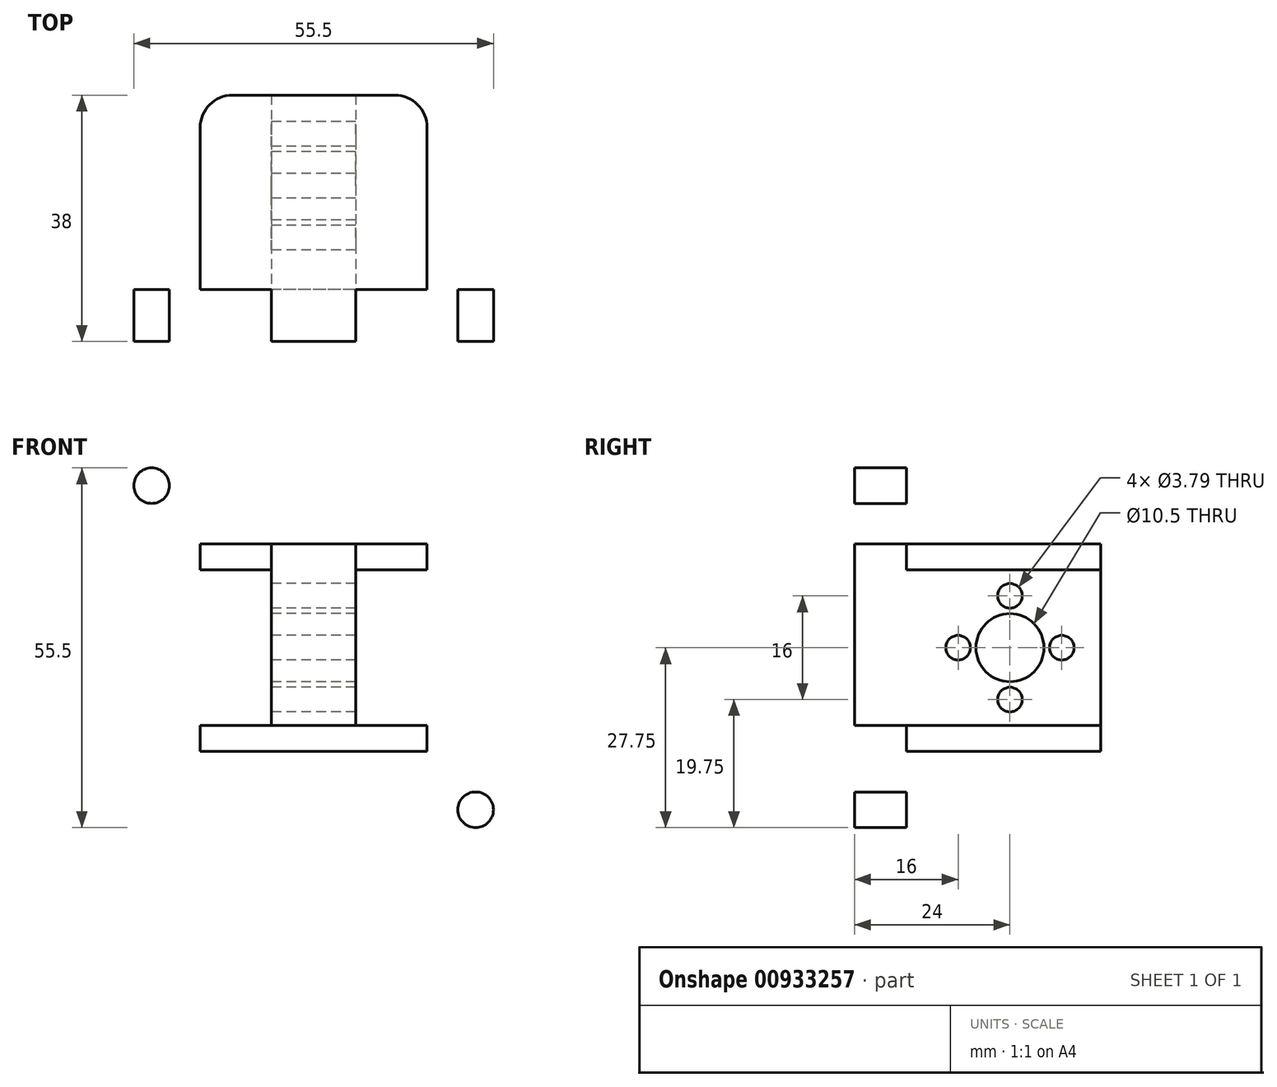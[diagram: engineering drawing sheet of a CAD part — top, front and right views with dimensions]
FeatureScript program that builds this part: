
annotation { "Feature Type Name" : "Feature", "Feature Type Description" : "" }
export const myFeature = defineFeature(function(context is Context, id is Id, definition is map)
    precondition{}
    {
        {
            var Q0;
            Q0=qCreatedBy(makeId("Front.planeOp"),FACE);
            var sketch = newSketch(context, id + "F0", { "sketchPlane" : qUnion([Q0])});
            skLineSegment(sketch, "E0.bottom", {"start": v(0, 0) * mm, "end": v(70, 0) * mm});
            skLineSegment(sketch, "E0.top", {"start": v(0, 130) * mm, "end": v(70, 130) * mm});
            skLineSegment(sketch, "E0.left", {"start": v(0, 0) * mm, "end": v(0, 130) * mm});
            skLineSegment(sketch, "E0.right", {"start": v(70, 0) * mm, "end": v(70, 130) * mm});
            skLineSegment(sketch, "E1", {"start": v(0, 125.15) * mm, "end": v(70, 125.15) * mm, "construction": true});
            skLineSegment(sketch, "E2", {"start": v(0, 101.15) * mm, "end": v(70, 101.15) * mm, "construction": true});
            skLineSegment(sketch, "E3", {"start": v(24, 130) * mm, "end": v(24, 78.99) * mm, "construction": true});
            skLineSegment(sketch, "E4", {"start": v(6, 130) * mm, "end": v(6, 79.2) * mm, "construction": true});
            skLineSegment(sketch, "E5", {"start": v(35, 130) * mm, "end": v(35, 0) * mm, "construction": true});
            skCircle(sketch, "E6", {"center": v(6, 125.15) * mm, "radius": 2.25 * mm});
            skCircle(sketch, "E7", {"center": v(24, 125.15) * mm, "radius": 2.25 * mm});
            skCircle(sketch, "E8", {"center": v(24, 101.15) * mm, "radius": 2.25 * mm});
            skCircle(sketch, "E9", {"center": v(6, 101.15) * mm, "radius": 2.25 * mm});
            skCircle(sketch, "E10.MirrorC", {"center": v(46, 101.15) * mm, "radius": 2.25 * mm});
            skCircle(sketch, "E11.MirrorC", {"center": v(64, 101.15) * mm, "radius": 2.25 * mm});
            skCircle(sketch, "E12.MirrorC", {"center": v(64, 125.15) * mm, "radius": 2.25 * mm});
            skCircle(sketch, "E13.MirrorC", {"center": v(46, 125.15) * mm, "radius": 2.25 * mm});
            skLineSegment(sketch, "E14", {"start": v(0, 65) * mm, "end": v(70, 65) * mm, "construction": true});
            skCircle(sketch, "E15.MirrorC", {"center": v(6, 28.85) * mm, "radius": 2.25 * mm});
            skCircle(sketch, "E16.MirrorC", {"center": v(24, 28.85) * mm, "radius": 2.25 * mm});
            skCircle(sketch, "E17.MirrorC", {"center": v(64, 28.85) * mm, "radius": 2.25 * mm});
            skCircle(sketch, "E18.MirrorC", {"center": v(46, 28.85) * mm, "radius": 2.25 * mm});
            skCircle(sketch, "E19.MirrorC", {"center": v(46, 4.85) * mm, "radius": 2.25 * mm});
            skCircle(sketch, "E20.MirrorC", {"center": v(64, 4.85) * mm, "radius": 2.25 * mm});
            skCircle(sketch, "E21.MirrorC", {"center": v(24, 4.85) * mm, "radius": 2.25 * mm});
            skCircle(sketch, "E22.MirrorC", {"center": v(6, 4.85) * mm, "radius": 2.25 * mm});
            skSolve(sketch);
        }
        {
            var Q0;
            Q0=makeQuery(id+"F0.imprint","IMPRINT",FACE,{"disambiguationData":[TD([[makeQuery(id+"F0.imprint","IMPRINT",EDGE,{"derivedFrom":sQuery(id+"F0.wireOp",EDGE,"E0.bottom")}),1.0]])]});
            extrude(context, id + "F1", {"entities" : qUnion([Q0]), "oppositeDirection" : true, "depth" : 8 * mm, "offsetDistance" : 25 * mm});
        }
        {
            var Q0;
            Q0=makeQuery(id+"F1.opExtrude","CAP_FACE",FACE,{"disambiguationData":[OSD([sQuery(id+"F0.wireOp",EDGE,"E0.bottom"),sQuery(id+"F0.wireOp",EDGE,"E0.top"),sQuery(id+"F0.wireOp",EDGE,"E0.left"),sQuery(id+"F0.wireOp",EDGE,"E0.right"),sQuery(id+"F0.wireOp",EDGE,"E6"),sQuery(id+"F0.wireOp",EDGE,"E7"),sQuery(id+"F0.wireOp",EDGE,"E8"),sQuery(id+"F0.wireOp",EDGE,"E9"),sQuery(id+"F0.wireOp",EDGE,"E10.MirrorC"),sQuery(id+"F0.wireOp",EDGE,"E11.MirrorC"),sQuery(id+"F0.wireOp",EDGE,"E12.MirrorC"),sQuery(id+"F0.wireOp",EDGE,"E13.MirrorC"),sQuery(id+"F0.wireOp",EDGE,"E15.MirrorC"),sQuery(id+"F0.wireOp",EDGE,"E16.MirrorC"),sQuery(id+"F0.wireOp",EDGE,"E17.MirrorC"),sQuery(id+"F0.wireOp",EDGE,"E18.MirrorC"),sQuery(id+"F0.wireOp",EDGE,"E19.MirrorC"),sQuery(id+"F0.wireOp",EDGE,"E20.MirrorC"),sQuery(id+"F0.wireOp",EDGE,"E21.MirrorC"),sQuery(id+"F0.wireOp",EDGE,"E22.MirrorC")])],"isStart":true});
            var sketch = newSketch(context, id + "F2", { "sketchPlane" : qUnion([Q0])});
            skCircle(sketch, "E23", {"center": v(6, 125.15) * mm, "radius": 3.75 * mm});
            skCircle(sketch, "E24", {"center": v(24, 125.15) * mm, "radius": 3.75 * mm});
            skCircle(sketch, "E25", {"center": v(6, 101.15) * mm, "radius": 3.75 * mm});
            skCircle(sketch, "E26", {"center": v(24, 101.15) * mm, "radius": 3.75 * mm});
            skLineSegment(sketch, "E27", {"start": v(35, 130) * mm, "end": v(35, 0) * mm});
            skLineSegment(sketch, "E28", {"start": v(0, 65) * mm, "end": v(70, 65) * mm});
            skCircle(sketch, "E29.MirrorC", {"center": v(46, 101.15) * mm, "radius": 3.75 * mm});
            skCircle(sketch, "E30.MirrorC", {"center": v(64, 101.15) * mm, "radius": 3.75 * mm});
            skCircle(sketch, "E31.MirrorC", {"center": v(46, 125.15) * mm, "radius": 3.75 * mm});
            skCircle(sketch, "E32.MirrorC", {"center": v(64, 125.15) * mm, "radius": 3.75 * mm});
            skCircle(sketch, "E33.MirrorC", {"center": v(6, 28.85) * mm, "radius": 3.75 * mm});
            skCircle(sketch, "E34.MirrorC", {"center": v(24, 28.85) * mm, "radius": 3.75 * mm});
            skCircle(sketch, "E35.MirrorC", {"center": v(46, 28.85) * mm, "radius": 3.75 * mm});
            skCircle(sketch, "E36.MirrorC", {"center": v(64, 28.85) * mm, "radius": 3.75 * mm});
            skCircle(sketch, "E37.MirrorC", {"center": v(64, 4.85) * mm, "radius": 3.75 * mm});
            skCircle(sketch, "E38.MirrorC", {"center": v(46, 4.85) * mm, "radius": 3.75 * mm});
            skCircle(sketch, "E39.MirrorC", {"center": v(24, 4.85) * mm, "radius": 3.75 * mm});
            skCircle(sketch, "E40.MirrorC", {"center": v(6, 4.85) * mm, "radius": 3.75 * mm});
            skSolve(sketch);
        }
        {
            var Q0;
            Q0=makeQuery(id+"F1.opExtrude","CAP_FACE",FACE,{"disambiguationData":[OSD([sQuery(id+"F0.wireOp",EDGE,"E0.bottom"),sQuery(id+"F0.wireOp",EDGE,"E0.top"),sQuery(id+"F0.wireOp",EDGE,"E0.left"),sQuery(id+"F0.wireOp",EDGE,"E0.right"),sQuery(id+"F0.wireOp",EDGE,"E6"),sQuery(id+"F0.wireOp",EDGE,"E7"),sQuery(id+"F0.wireOp",EDGE,"E8"),sQuery(id+"F0.wireOp",EDGE,"E9"),sQuery(id+"F0.wireOp",EDGE,"E10.MirrorC"),sQuery(id+"F0.wireOp",EDGE,"E11.MirrorC"),sQuery(id+"F0.wireOp",EDGE,"E12.MirrorC"),sQuery(id+"F0.wireOp",EDGE,"E13.MirrorC"),sQuery(id+"F0.wireOp",EDGE,"E15.MirrorC"),sQuery(id+"F0.wireOp",EDGE,"E16.MirrorC"),sQuery(id+"F0.wireOp",EDGE,"E17.MirrorC"),sQuery(id+"F0.wireOp",EDGE,"E18.MirrorC"),sQuery(id+"F0.wireOp",EDGE,"E19.MirrorC"),sQuery(id+"F0.wireOp",EDGE,"E20.MirrorC"),sQuery(id+"F0.wireOp",EDGE,"E21.MirrorC"),sQuery(id+"F0.wireOp",EDGE,"E22.MirrorC")])],"isStart":false});
            var sketch = newSketch(context, id + "F3", { "sketchPlane" : qUnion([Q0])});
            skLineSegment(sketch, "E41.bottom", {"start": v(-28.5, 53) * mm, "end": v(-41.5, 53) * mm});
            skLineSegment(sketch, "E41.top", {"start": v(-28.5, 77) * mm, "end": v(-41.5, 77) * mm});
            skLineSegment(sketch, "E41.left", {"start": v(-28.5, 53) * mm, "end": v(-28.5, 77) * mm});
            skLineSegment(sketch, "E41.right", {"start": v(-41.5, 53) * mm, "end": v(-41.5, 77) * mm});
            skPoint(sketch, "E41.middle", {"position": v(-35, 65) * mm});
            skSolve(sketch);
        }
        {
            var Q0;
            Q0=makeQuery(id+"F3.imprint","IMPRINT",FACE,{"disambiguationData":[TD([[makeQuery(id+"F3.imprint","IMPRINT",EDGE,{"derivedFrom":sQuery(id+"F3.wireOp",EDGE,"E41.bottom")}),-1.0]])]});
            extrude(context, id + "F4", {"entities" : qUnion([Q0]), "operationType" : NewBodyOperationType.ADD, "depth" : 30 * mm, "offsetDistance" : 25 * mm});
        }
        {
            var Q0;
            Q0=makeQuery(id+"F4.opExtrude","SWEPT_FACE",FACE,{"disambiguationData":[OSD([sQuery(id+"F3.wireOp",EDGE,"E41.left")])]});
            var sketch = newSketch(context, id + "F5", { "sketchPlane" : qUnion([Q0])});
            skLineSegment(sketch, "E42", {"start": v(-24, 81.62) * mm, "end": v(-24, 48.38) * mm, "construction": true});
            skLineSegment(sketch, "E43", {"start": v(-38, 65) * mm, "end": v(-8, 65) * mm, "construction": true});
            skCircle(sketch, "E44", {"center": v(-24, 65) * mm, "radius": 5.25 * mm});
            skPoint(sketch, "E44.centerSnap0", {"position": v(-24, 65) * mm});
            skCircle(sketch, "E45", {"center": v(-24, 65) * mm, "radius": 11.1 * mm, "construction": true});
            skCircle(sketch, "E46", {"center": v(-24, 65) * mm, "radius": 8 * mm, "construction": true});
            skCircle(sketch, "E47", {"center": v(-24, 73) * mm, "radius": 1.9 * mm});
            skCircle(sketch, "E48.1.0", {"center": v(-32, 65) * mm, "radius": 1.9 * mm});
            skCircle(sketch, "E48.2.0", {"center": v(-24, 57) * mm, "radius": 1.9 * mm});
            skCircle(sketch, "E48.3.0", {"center": v(-16, 65) * mm, "radius": 1.9 * mm});
            skSolve(sketch);
        }
        {
            var Q0;
            Q0=makeQuery(id+"F5.imprint","IMPRINT",FACE,{"disambiguationData":[TD([[makeQuery(id+"F5.imprint","IMPRINT",EDGE,{"derivedFrom":sQuery(id+"F5.wireOp",EDGE,"E48.1.0")}),1.0]])]});
            var Q1;
            Q1=makeQuery(id+"F5.imprint","IMPRINT",FACE,{"disambiguationData":[TD([[makeQuery(id+"F5.imprint","IMPRINT",EDGE,{"derivedFrom":sQuery(id+"F5.wireOp",EDGE,"E47")}),1.0]])]});
            var Q2;
            Q2=makeQuery(id+"F5.imprint","IMPRINT",FACE,{"disambiguationData":[TD([[makeQuery(id+"F5.imprint","IMPRINT",EDGE,{"derivedFrom":sQuery(id+"F5.wireOp",EDGE,"E48.3.0")}),1.0]])]});
            var Q3;
            Q3=makeQuery(id+"F5.imprint","IMPRINT",FACE,{"disambiguationData":[TD([[makeQuery(id+"F5.imprint","IMPRINT",EDGE,{"derivedFrom":sQuery(id+"F5.wireOp",EDGE,"E48.2.0")}),1.0]])]});
            var Q4;
            Q4=makeQuery(id+"F5.imprint","IMPRINT",FACE,{"disambiguationData":[TD([[makeQuery(id+"F5.imprint","IMPRINT",EDGE,{"derivedFrom":sQuery(id+"F5.wireOp",EDGE,"E44")}),1.0]])]});
            extrude(context, id + "F6", {"entities" : qUnion([Q0, Q1, Q2, Q3, Q4]), "operationType" : NewBodyOperationType.REMOVE, "endBound" : BoundingType.THROUGH_ALL, "oppositeDirection" : true, "depth" : 25 * mm, "offsetDistance" : 25 * mm});
        }
        {
            var Q0;
            Q0=makeQuery(id+"F1.opExtrude","CAP_FACE",FACE,{"disambiguationData":[OSD([sQuery(id+"F0.wireOp",EDGE,"E0.bottom"),sQuery(id+"F0.wireOp",EDGE,"E0.top"),sQuery(id+"F0.wireOp",EDGE,"E0.left"),sQuery(id+"F0.wireOp",EDGE,"E0.right"),sQuery(id+"F0.wireOp",EDGE,"E6"),sQuery(id+"F0.wireOp",EDGE,"E7"),sQuery(id+"F0.wireOp",EDGE,"E8"),sQuery(id+"F0.wireOp",EDGE,"E9"),sQuery(id+"F0.wireOp",EDGE,"E10.MirrorC"),sQuery(id+"F0.wireOp",EDGE,"E11.MirrorC"),sQuery(id+"F0.wireOp",EDGE,"E12.MirrorC"),sQuery(id+"F0.wireOp",EDGE,"E13.MirrorC"),sQuery(id+"F0.wireOp",EDGE,"E15.MirrorC"),sQuery(id+"F0.wireOp",EDGE,"E16.MirrorC"),sQuery(id+"F0.wireOp",EDGE,"E17.MirrorC"),sQuery(id+"F0.wireOp",EDGE,"E18.MirrorC"),sQuery(id+"F0.wireOp",EDGE,"E19.MirrorC"),sQuery(id+"F0.wireOp",EDGE,"E20.MirrorC"),sQuery(id+"F0.wireOp",EDGE,"E21.MirrorC"),sQuery(id+"F0.wireOp",EDGE,"E22.MirrorC")])],"isStart":false});
            var sketch = newSketch(context, id + "F7", { "sketchPlane" : qUnion([Q0])});
            skLineSegment(sketch, "E49", {"start": v(-60, 130) * mm, "end": v(-60, 0) * mm, "construction": true});
            skLineSegment(sketch, "E50", {"start": v(-70, 90) * mm, "end": v(0, 90) * mm, "construction": true});
            skCircle(sketch, "E51", {"center": v(-60, 90) * mm, "radius": 2.75 * mm});
            skCircle(sketch, "E52.MirrorC", {"center": v(-10, 90) * mm, "radius": 2.75 * mm});
            skCircle(sketch, "E53.MirrorC", {"center": v(-10, 40) * mm, "radius": 2.75 * mm});
            skCircle(sketch, "E54.MirrorC", {"center": v(-60, 40) * mm, "radius": 2.75 * mm});
            skSolve(sketch);
        }
        {
            var Q0;
            Q0=makeQuery(id+"F7.imprint","IMPRINT",FACE,{"disambiguationData":[TD([[makeQuery(id+"F7.imprint","IMPRINT",EDGE,{"derivedFrom":sQuery(id+"F7.wireOp",EDGE,"E51")}),1.0]])]});
            var Q1;
            Q1=makeQuery(id+"F7.imprint","IMPRINT",FACE,{"disambiguationData":[TD([[makeQuery(id+"F7.imprint","IMPRINT",EDGE,{"derivedFrom":sQuery(id+"F7.wireOp",EDGE,"E52.MirrorC")}),-1.0]])]});
            var Q2;
            Q2=makeQuery(id+"F7.imprint","IMPRINT",FACE,{"disambiguationData":[TD([[makeQuery(id+"F7.imprint","IMPRINT",EDGE,{"derivedFrom":sQuery(id+"F7.wireOp",EDGE,"E54.MirrorC")}),-1.0]])]});
            var Q3;
            Q3=makeQuery(id+"F7.imprint","IMPRINT",FACE,{"disambiguationData":[TD([[makeQuery(id+"F7.imprint","IMPRINT",EDGE,{"derivedFrom":sQuery(id+"F7.wireOp",EDGE,"E53.MirrorC")}),1.0]])]});
            extrude(context, id + "F8", {"entities" : qUnion([Q0, Q1, Q2, Q3]), "operationType" : NewBodyOperationType.REMOVE, "endBound" : BoundingType.THROUGH_ALL, "oppositeDirection" : true, "depth" : 25 * mm, "offsetDistance" : 25 * mm});
        }
        {
            var Q0;
            Q0=makeQuery(id+"F1.opExtrude","CAP_FACE",FACE,{"disambiguationData":[OSD([sQuery(id+"F0.wireOp",EDGE,"E0.bottom"),sQuery(id+"F0.wireOp",EDGE,"E0.top"),sQuery(id+"F0.wireOp",EDGE,"E0.left"),sQuery(id+"F0.wireOp",EDGE,"E0.right"),sQuery(id+"F0.wireOp",EDGE,"E6"),sQuery(id+"F0.wireOp",EDGE,"E7"),sQuery(id+"F0.wireOp",EDGE,"E8"),sQuery(id+"F0.wireOp",EDGE,"E9"),sQuery(id+"F0.wireOp",EDGE,"E10.MirrorC"),sQuery(id+"F0.wireOp",EDGE,"E11.MirrorC"),sQuery(id+"F0.wireOp",EDGE,"E12.MirrorC"),sQuery(id+"F0.wireOp",EDGE,"E13.MirrorC"),sQuery(id+"F0.wireOp",EDGE,"E15.MirrorC"),sQuery(id+"F0.wireOp",EDGE,"E16.MirrorC"),sQuery(id+"F0.wireOp",EDGE,"E17.MirrorC"),sQuery(id+"F0.wireOp",EDGE,"E18.MirrorC"),sQuery(id+"F0.wireOp",EDGE,"E19.MirrorC"),sQuery(id+"F0.wireOp",EDGE,"E20.MirrorC"),sQuery(id+"F0.wireOp",EDGE,"E21.MirrorC"),sQuery(id+"F0.wireOp",EDGE,"E22.MirrorC")])],"isStart":false});
            var sketch = newSketch(context, id + "F9", { "sketchPlane" : qUnion([Q0])});
            skCircle(sketch, "E55", {"center": v(-60, 90) * mm, "radius": 5 * mm});
            skCircle(sketch, "E56.MirrorC", {"center": v(-10, 90) * mm, "radius": 5 * mm});
            skCircle(sketch, "E57.MirrorC", {"center": v(-10, 40) * mm, "radius": 5 * mm});
            skCircle(sketch, "E58.MirrorC", {"center": v(-60, 40) * mm, "radius": 5 * mm});
            skSolve(sketch);
        }
        {
            var Q0;
            Q0=makeQuery(id+"F9.imprint","IMPRINT",FACE,{"disambiguationData":[TD([[makeQuery(id+"F9.imprint","IMPRINT",EDGE,{"derivedFrom":sQuery(id+"F9.wireOp",EDGE,"E55")}),1.0]])]});
            var Q1;
            Q1=makeQuery(id+"F9.imprint","IMPRINT",FACE,{"disambiguationData":[TD([[makeQuery(id+"F9.imprint","IMPRINT",EDGE,{"derivedFrom":sQuery(id+"F9.wireOp",EDGE,"E56.MirrorC")}),-1.0]])]});
            var Q2;
            Q2=makeQuery(id+"F9.imprint","IMPRINT",FACE,{"disambiguationData":[TD([[makeQuery(id+"F9.imprint","IMPRINT",EDGE,{"derivedFrom":sQuery(id+"F9.wireOp",EDGE,"E57.MirrorC")}),1.0]])]});
            var Q3;
            Q3=makeQuery(id+"F9.imprint","IMPRINT",FACE,{"disambiguationData":[TD([[makeQuery(id+"F9.imprint","IMPRINT",EDGE,{"derivedFrom":sQuery(id+"F9.wireOp",EDGE,"E58.MirrorC")}),-1.0]])]});
            extrude(context, id + "F10", {"entities" : qUnion([Q0, Q1, Q2, Q3]), "operationType" : NewBodyOperationType.REMOVE, "oppositeDirection" : true, "depth" : 5 * mm, "offsetDistance" : 25 * mm});
        }
        {
            var Q0;
            Q0=makeQuery(id+"F4.opExtrude","SWEPT_FACE",FACE,{"disambiguationData":[OSD([sQuery(id+"F3.wireOp",EDGE,"E41.top")])]});
            var sketch = newSketch(context, id + "F11", { "sketchPlane" : qUnion([Q0])});
            skLineSegment(sketch, "E59", {"start": v(41.5, 38) * mm, "end": v(28.5, 38) * mm});
            skLineSegment(sketch, "E60.bottom", {"start": v(28.5, 38) * mm, "end": v(22.5, 38) * mm});
            skLineSegment(sketch, "E60.top", {"start": v(28.5, 8) * mm, "end": v(17.5, 8) * mm});
            skLineSegment(sketch, "E60.left", {"start": v(28.5, 38) * mm, "end": v(28.5, 8) * mm});
            skLineSegment(sketch, "E60.right", {"start": v(17.5, 33) * mm, "end": v(17.5, 8) * mm});
            skPoint(sketch, "E61.visualSharp", {"position": v(17.5, 38) * mm});
            skArc(sketch, "E61.filletArc", {"start": v(22.5, 38) * mm, "mid": v(18.96, 36.54) * mm, "end": v(17.5, 33) * mm});
            skLineSegment(sketch, "E62", {"start": v(35, 38) * mm, "end": v(35, 8) * mm, "construction": true});
            skLineSegment(sketch, "E63.MirrorCS", {"start": v(41.5, 38) * mm, "end": v(41.5, 8) * mm});
            skLineSegment(sketch, "E64.MirrorCS", {"start": v(41.5, 8) * mm, "end": v(52.5, 8) * mm});
            skLineSegment(sketch, "E65.MirrorCS", {"start": v(41.5, 38) * mm, "end": v(47.5, 38) * mm});
            skLineSegment(sketch, "E66.MirrorCS", {"start": v(52.5, 33) * mm, "end": v(52.5, 8) * mm});
            skArc(sketch, "E67.MirrorCS", {"start": v(47.5, 38) * mm, "mid": v(51.04, 36.54) * mm, "end": v(52.5, 33) * mm});
            skSolve(sketch);
        }
        {
            var Q0;
            {var subQ0=sQuery(id+"F11.wireOp",EDGE,"xESoRonm-LhQB-Ssj1-jqFH-StdoRr2X7NTl");Q0=makeQuery(id+"F11.imprint","IMPRINT",FACE,{"disambiguationData":[TD([[makeQuery(id+"F11.imprint","IMPRINT",EDGE,{"derivedFrom":subQ0}),1.0]])]});}
            var Q1;
            {var subQ6=sQuery(id+"F11.wireOp",EDGE,"E59");Q1=makeQuery(id+"F11.imprint","IMPRINT",FACE,{"disambiguationData":[TD([[makeQuery(id+"F11.imprint","IMPRINT",EDGE,{"derivedFrom":subQ6}),-1.0]])]});}
            var Q2;
            {var subQ0=sQuery(id+"F11.wireOp",EDGE,"kL0RBXTn-8g1l-G1Ez-Omut-TmTzhNwdl61b");Q2=makeQuery(id+"F11.imprint","IMPRINT",FACE,{"disambiguationData":[TD([[makeQuery(id+"F11.imprint","IMPRINT",EDGE,{"derivedFrom":subQ0}),1.0]])]});}
            extrude(context, id + "F12", {"entities" : qUnion([Q0, Q1, Q2]), "operationType" : NewBodyOperationType.ADD, "depth" : 4 * mm, "offsetDistance" : 25 * mm});
        }
        {
            var Q0;
            Q0=makeQuery(id+"F4.opExtrude","SWEPT_FACE",FACE,{"disambiguationData":[OSD([sQuery(id+"F3.wireOp",EDGE,"E41.bottom")])]});
            var sketch = newSketch(context, id + "F13", { "sketchPlane" : qUnion([Q0])});
            skLineSegment(sketch, "E68", {"start": v(52.5, -8) * mm, "end": v(17.5, -8) * mm});
            skLineSegment(sketch, "E69", {"start": v(28.5, -38) * mm, "end": v(41.5, -38) * mm});
            skLineSegment(sketch, "E70", {"start": v(35, -38) * mm, "end": v(35, -8) * mm, "construction": true});
            skLineSegment(sketch, "E71.bottom", {"start": v(41.5, -38) * mm, "end": v(47.5, -38) * mm});
            skLineSegment(sketch, "E71.top", {"start": v(41.5, -8) * mm, "end": v(52.5, -8) * mm});
            skLineSegment(sketch, "E71.left", {"start": v(41.5, -38) * mm, "end": v(41.5, -8) * mm});
            skLineSegment(sketch, "E71.right", {"start": v(52.5, -33) * mm, "end": v(52.5, -8) * mm});
            skLineSegment(sketch, "E72.MirrorCS", {"start": v(28.5, -8) * mm, "end": v(17.5, -8) * mm});
            skLineSegment(sketch, "E73.MirrorCS", {"start": v(28.5, -38) * mm, "end": v(22.5, -38) * mm});
            skPoint(sketch, "E74.orphan", {"position": v(0, -8) * mm});
            skPoint(sketch, "E75.visualSharp", {"position": v(52.5, -38) * mm});
            skArc(sketch, "E75.filletArc", {"start": v(47.5, -38) * mm, "mid": v(51.04, -36.54) * mm, "end": v(52.5, -33) * mm});
            skPoint(sketch, "E76.visualSharp", {"position": v(17.5, -38) * mm});
            skLineSegment(sketch, "E77.MirrorCS", {"start": v(28.5, -38) * mm, "end": v(28.5, -8) * mm});
            skLineSegment(sketch, "E78.MirrorCS", {"start": v(17.5, -33) * mm, "end": v(17.5, -8) * mm});
            skArc(sketch, "E79.MirrorCS", {"start": v(22.5, -38) * mm, "mid": v(18.96, -36.54) * mm, "end": v(17.5, -33) * mm});
            skSolve(sketch);
        }
        {
            var Q0;
            {var subQ0=sQuery(id+"F13.wireOp",EDGE,"hdJWUI9M-KXb4-t5Z4-sRnf-rSk5xYNh7SRG");Q0=makeQuery(id+"F13.imprint","IMPRINT",FACE,{"disambiguationData":[TD([[makeQuery(id+"F13.imprint","IMPRINT",EDGE,{"derivedFrom":subQ0}),1.0]])]});}
            var Q1;
            {var subQ6=sQuery(id+"F13.wireOp",EDGE,"E69");Q1=makeQuery(id+"F13.imprint","IMPRINT",FACE,{"disambiguationData":[TD([[makeQuery(id+"F13.imprint","IMPRINT",EDGE,{"derivedFrom":subQ6}),1.0]])]});}
            var Q2;
            {var subQ0=sQuery(id+"F13.wireOp",EDGE,"G3PmWDNW-oeGG-h8XP-9mMC-rU47nYxFmo2q");Q2=makeQuery(id+"F13.imprint","IMPRINT",FACE,{"disambiguationData":[TD([[makeQuery(id+"F13.imprint","IMPRINT",EDGE,{"derivedFrom":subQ0}),1.0]])]});}
            extrude(context, id + "F14", {"entities" : qUnion([Q0, Q1, Q2]), "operationType" : NewBodyOperationType.ADD, "depth" : 4 * mm, "offsetDistance" : 25 * mm});
        }
        {
            var Q0;
            Q0=makeQuery(id+"F1.opExtrude","CAP_FACE",FACE,{"disambiguationData":[OSD([sQuery(id+"F0.wireOp",EDGE,"E0.bottom"),sQuery(id+"F0.wireOp",EDGE,"E0.top"),sQuery(id+"F0.wireOp",EDGE,"E0.left"),sQuery(id+"F0.wireOp",EDGE,"E0.right"),sQuery(id+"F0.wireOp",EDGE,"E6"),sQuery(id+"F0.wireOp",EDGE,"E7"),sQuery(id+"F0.wireOp",EDGE,"E8"),sQuery(id+"F0.wireOp",EDGE,"E9"),sQuery(id+"F0.wireOp",EDGE,"E10.MirrorC"),sQuery(id+"F0.wireOp",EDGE,"E11.MirrorC"),sQuery(id+"F0.wireOp",EDGE,"E12.MirrorC"),sQuery(id+"F0.wireOp",EDGE,"E13.MirrorC"),sQuery(id+"F0.wireOp",EDGE,"E15.MirrorC"),sQuery(id+"F0.wireOp",EDGE,"E16.MirrorC"),sQuery(id+"F0.wireOp",EDGE,"E17.MirrorC"),sQuery(id+"F0.wireOp",EDGE,"E18.MirrorC"),sQuery(id+"F0.wireOp",EDGE,"E19.MirrorC"),sQuery(id+"F0.wireOp",EDGE,"E20.MirrorC"),sQuery(id+"F0.wireOp",EDGE,"E21.MirrorC"),sQuery(id+"F0.wireOp",EDGE,"E22.MirrorC")])],"isStart":true});
            var sketch = newSketch(context, id + "F15", { "sketchPlane" : qUnion([Q0])});
            skCircle(sketch, "E80", {"center": v(6, 125.15) * mm, "radius": 3.75 * mm});
            skCircle(sketch, "E81", {"center": v(24, 125.15) * mm, "radius": 3.75 * mm});
            skCircle(sketch, "E82", {"center": v(6, 101.15) * mm, "radius": 3.75 * mm});
            skCircle(sketch, "E83", {"center": v(24, 101.15) * mm, "radius": 3.75 * mm});
            skLineSegment(sketch, "E84", {"start": v(35, 130) * mm, "end": v(35, 0) * mm, "construction": true});
            skLineSegment(sketch, "E85", {"start": v(0, 65) * mm, "end": v(70, 65) * mm, "construction": true});
            skCircle(sketch, "E86.MirrorC", {"center": v(46, 101.15) * mm, "radius": 3.75 * mm});
            skCircle(sketch, "E87.MirrorC", {"center": v(64, 101.15) * mm, "radius": 3.75 * mm});
            skCircle(sketch, "E88.MirrorC", {"center": v(46, 125.15) * mm, "radius": 3.75 * mm});
            skCircle(sketch, "E89.MirrorC", {"center": v(64, 125.15) * mm, "radius": 3.75 * mm});
            skCircle(sketch, "E90.MirrorC", {"center": v(6, 28.85) * mm, "radius": 3.75 * mm});
            skCircle(sketch, "E91.MirrorC", {"center": v(24, 28.85) * mm, "radius": 3.75 * mm});
            skCircle(sketch, "E92.MirrorC", {"center": v(46, 28.85) * mm, "radius": 3.75 * mm});
            skCircle(sketch, "E93.MirrorC", {"center": v(64, 28.85) * mm, "radius": 3.75 * mm});
            skCircle(sketch, "E94.MirrorC", {"center": v(64, 4.85) * mm, "radius": 3.75 * mm});
            skCircle(sketch, "E95.MirrorC", {"center": v(46, 4.85) * mm, "radius": 3.75 * mm});
            skCircle(sketch, "E96.MirrorC", {"center": v(24, 4.85) * mm, "radius": 3.75 * mm});
            skCircle(sketch, "E97.MirrorC", {"center": v(6, 4.85) * mm, "radius": 3.75 * mm});
            skSolve(sketch);
        }
        {
            var Q0;
            Q0=makeQuery(id+"F15.imprint","IMPRINT",FACE,{"disambiguationData":[TD([[makeQuery(id+"F15.imprint","IMPRINT",EDGE,{"derivedFrom":sQuery(id+"F15.wireOp",EDGE,"E80")}),1.0]])]});
            var Q1;
            Q1=makeQuery(id+"F15.imprint","IMPRINT",FACE,{"disambiguationData":[TD([[makeQuery(id+"F15.imprint","IMPRINT",EDGE,{"derivedFrom":sQuery(id+"F15.wireOp",EDGE,"E83")}),1.0]])]});
            var Q2;
            Q2=makeQuery(id+"F15.imprint","IMPRINT",FACE,{"disambiguationData":[TD([[makeQuery(id+"F15.imprint","IMPRINT",EDGE,{"derivedFrom":sQuery(id+"F15.wireOp",EDGE,"E81")}),1.0]])]});
            var Q3;
            Q3=makeQuery(id+"F15.imprint","IMPRINT",FACE,{"disambiguationData":[TD([[makeQuery(id+"F15.imprint","IMPRINT",EDGE,{"derivedFrom":sQuery(id+"F15.wireOp",EDGE,"E82")}),1.0]])]});
            var Q4;
            Q4=makeQuery(id+"F15.imprint","IMPRINT",FACE,{"disambiguationData":[TD([[makeQuery(id+"F15.imprint","IMPRINT",EDGE,{"derivedFrom":sQuery(id+"F15.wireOp",EDGE,"E88.MirrorC")}),-1.0]])]});
            var Q5;
            Q5=makeQuery(id+"F15.imprint","IMPRINT",FACE,{"disambiguationData":[TD([[makeQuery(id+"F15.imprint","IMPRINT",EDGE,{"derivedFrom":sQuery(id+"F15.wireOp",EDGE,"E89.MirrorC")}),-1.0]])]});
            var Q6;
            Q6=makeQuery(id+"F15.imprint","IMPRINT",FACE,{"disambiguationData":[TD([[makeQuery(id+"F15.imprint","IMPRINT",EDGE,{"derivedFrom":sQuery(id+"F15.wireOp",EDGE,"E86.MirrorC")}),-1.0]])]});
            var Q7;
            Q7=makeQuery(id+"F15.imprint","IMPRINT",FACE,{"disambiguationData":[TD([[makeQuery(id+"F15.imprint","IMPRINT",EDGE,{"derivedFrom":sQuery(id+"F15.wireOp",EDGE,"E87.MirrorC")}),-1.0]])]});
            var Q8;
            Q8=makeQuery(id+"F15.imprint","IMPRINT",FACE,{"disambiguationData":[TD([[makeQuery(id+"F15.imprint","IMPRINT",EDGE,{"derivedFrom":sQuery(id+"F15.wireOp",EDGE,"E90.MirrorC")}),-1.0]])]});
            var Q9;
            Q9=makeQuery(id+"F15.imprint","IMPRINT",FACE,{"disambiguationData":[TD([[makeQuery(id+"F15.imprint","IMPRINT",EDGE,{"derivedFrom":sQuery(id+"F15.wireOp",EDGE,"E91.MirrorC")}),-1.0]])]});
            var Q10;
            Q10=makeQuery(id+"F15.imprint","IMPRINT",FACE,{"disambiguationData":[TD([[makeQuery(id+"F15.imprint","IMPRINT",EDGE,{"derivedFrom":sQuery(id+"F15.wireOp",EDGE,"E92.MirrorC")}),1.0]])]});
            var Q11;
            Q11=makeQuery(id+"F15.imprint","IMPRINT",FACE,{"disambiguationData":[TD([[makeQuery(id+"F15.imprint","IMPRINT",EDGE,{"derivedFrom":sQuery(id+"F15.wireOp",EDGE,"E97.MirrorC")}),-1.0]])]});
            var Q12;
            Q12=makeQuery(id+"F15.imprint","IMPRINT",FACE,{"disambiguationData":[TD([[makeQuery(id+"F15.imprint","IMPRINT",EDGE,{"derivedFrom":sQuery(id+"F15.wireOp",EDGE,"E93.MirrorC")}),1.0]])]});
            var Q13;
            Q13=makeQuery(id+"F15.imprint","IMPRINT",FACE,{"disambiguationData":[TD([[makeQuery(id+"F15.imprint","IMPRINT",EDGE,{"derivedFrom":sQuery(id+"F15.wireOp",EDGE,"E96.MirrorC")}),-1.0]])]});
            var Q14;
            Q14=makeQuery(id+"F15.imprint","IMPRINT",FACE,{"disambiguationData":[TD([[makeQuery(id+"F15.imprint","IMPRINT",EDGE,{"derivedFrom":sQuery(id+"F15.wireOp",EDGE,"E95.MirrorC")}),1.0]])]});
            var Q15;
            Q15=makeQuery(id+"F15.imprint","IMPRINT",FACE,{"disambiguationData":[TD([[makeQuery(id+"F15.imprint","IMPRINT",EDGE,{"derivedFrom":sQuery(id+"F15.wireOp",EDGE,"E94.MirrorC")}),1.0]])]});
            var Q16;
            Q16=sQuery(id+"F15.wireOp",EDGE,"E80");
            var Q17;
            Q17=sQuery(id+"F15.wireOp",EDGE,"E81");
            var Q18;
            Q18=sQuery(id+"F15.wireOp",EDGE,"E83");
            var Q19;
            Q19=sQuery(id+"F15.wireOp",EDGE,"E82");
            extrude(context, id + "F16", {"entities" : qUnion([Q0, Q1, Q2, Q3, Q4, Q5, Q6, Q7, Q8, Q9, Q10, Q11, Q12, Q13, Q14, Q15]), "operationType" : NewBodyOperationType.REMOVE, "surfaceEntities" : qUnion([Q16, Q17, Q18, Q19]), "oppositeDirection" : true, "depth" : 5 * mm, "offsetDistance" : 25 * mm});
        }
        {
            var Q0;
            {var subQ1=sQuery(id+"F13.wireOp",EDGE,"E71.left");Q0=makeQuery(id+"F13.imprint","IMPRINT",FACE,{"disambiguationData":[TD([[makeQuery(id+"F13.imprint","IMPRINT",EDGE,{"derivedFrom":subQ1}),-1.0]])]});}
            var Q1;
            Q1=makeQuery(id+"F13.imprint","IMPRINT",FACE,{"disambiguationData":[TD([[makeQuery(id+"F13.imprint","IMPRINT",EDGE,{"derivedFrom":sQuery(id+"F13.wireOp",EDGE,"E77.MirrorCS")}),1.0]])]});
            extrude(context, id + "F17", {"entities" : qUnion([Q0, Q1]), "operationType" : NewBodyOperationType.ADD, "depth" : 4 * mm, "offsetDistance" : 25 * mm});
        }
        {
            var Q0;
            Q0=makeQuery(id+"F11.imprint","IMPRINT",FACE,{"disambiguationData":[TD([[makeQuery(id+"F11.imprint","IMPRINT",EDGE,{"derivedFrom":sQuery(id+"F11.wireOp",EDGE,"E60.bottom")}),1.0]])]});
            var Q1;
            Q1=makeQuery(id+"F11.imprint","IMPRINT",FACE,{"disambiguationData":[TD([[makeQuery(id+"F11.imprint","IMPRINT",EDGE,{"derivedFrom":sQuery(id+"F11.wireOp",EDGE,"E63.MirrorCS")}),1.0]])]});
            var Q2;
            Q2=makeQuery(id+"F11.imprint","IMPRINT",FACE,{"disambiguationData":[TD([[makeQuery(id+"F11.imprint","IMPRINT",EDGE,{"derivedFrom":sQuery(id+"F11.wireOp",EDGE,"E59")}),-1.0]])]});
            extrude(context, id + "F18", {"entities" : qUnion([Q0, Q1, Q2]), "operationType" : NewBodyOperationType.ADD, "depth" : 4 * mm, "offsetDistance" : 25 * mm});
        }
    });
